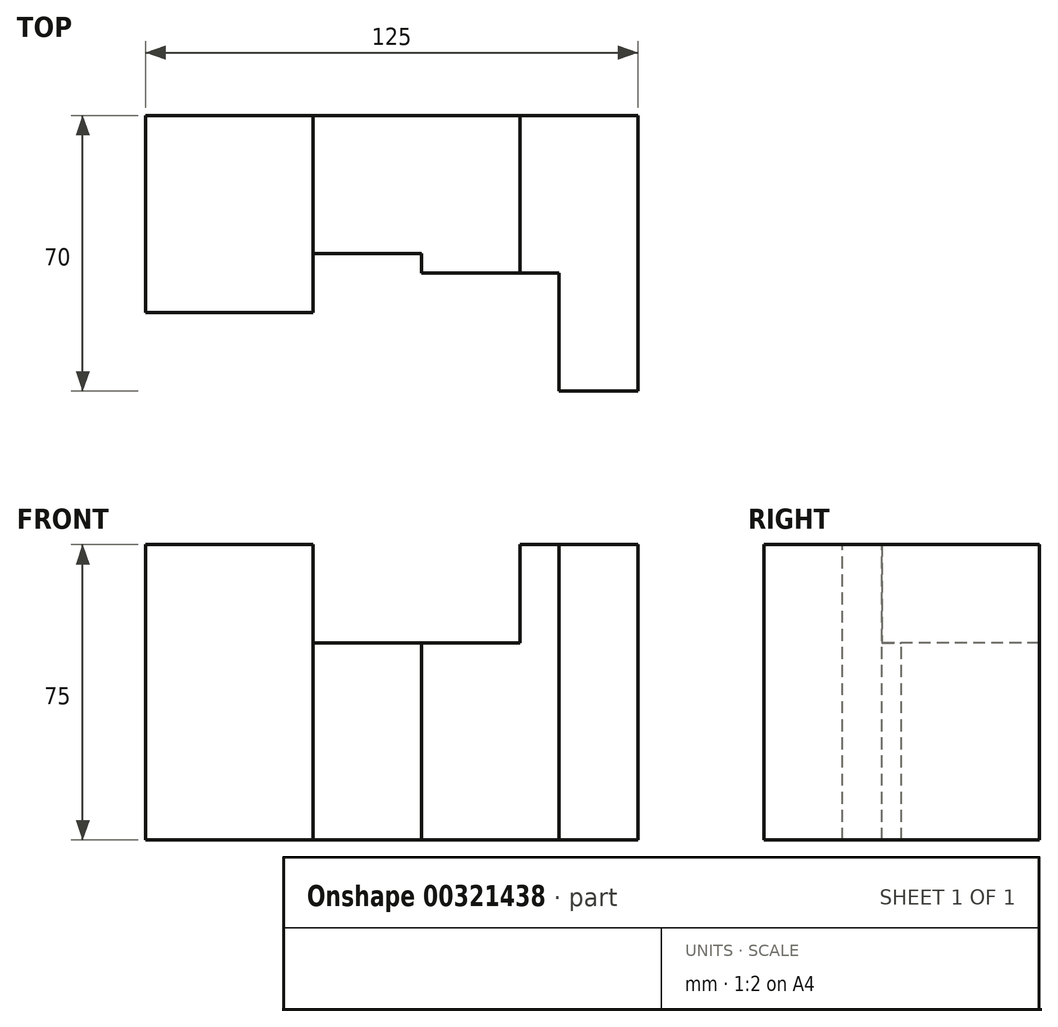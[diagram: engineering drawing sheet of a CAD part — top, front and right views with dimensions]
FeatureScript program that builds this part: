
annotation { "Feature Type Name" : "Feature", "Feature Type Description" : "" }
export const myFeature = defineFeature(function(context is Context, id is Id, definition is map)
    precondition{}
    {
        {
            var Q0;
            Q0=qCreatedBy(makeId("Front.planeOp"),FACE);
            var sketch = newSketch(context, id + "F0", { "sketchPlane" : qUnion([Q0])});
            skLineSegment(sketch, "E0.bottom", {"start": v(0, 0) * mm, "end": v(125, 0) * mm});
            skLineSegment(sketch, "E0.top", {"start": v(0, 75) * mm, "end": v(125, 75) * mm});
            skLineSegment(sketch, "E0.left", {"start": v(0, 0) * mm, "end": v(0, 75) * mm});
            skLineSegment(sketch, "E0.right", {"start": v(125, 0) * mm, "end": v(125, 75) * mm});
            skSolve(sketch);
        }
        {
            var Q0;
            Q0 = qSketchRegion(id + "F0", true);
            extrude(context, id + "F1", {"entities" : qUnion([Q0]), "depth" : (14 * 5) * mm});
        }
        {
            var Q0;
            Q0=makeQuery(id+"F1.opExtrude","SWEPT_FACE",FACE,{"disambiguationData":[OSD([sQuery(id+"F0.wireOp",EDGE,"E0.top")])]});
            var sketch = newSketch(context, id + "F2", { "sketchPlane" : qUnion([Q0])});
            skLineSegment(sketch, "E1.bottom", {"start": v(0, -70) * mm, "end": v(42.5, -70) * mm});
            skLineSegment(sketch, "E1.top", {"start": v(0, -50) * mm, "end": v(42.5, -50) * mm});
            skLineSegment(sketch, "E1.left", {"start": v(0, -70) * mm, "end": v(0, -50) * mm});
            skLineSegment(sketch, "E1.right", {"start": v(42.5, -70) * mm, "end": v(42.5, -50) * mm});
            skSolve(sketch);
        }
        {
            var Q0;
            Q0 = qSketchRegion(id + "F2", true);
            extrude(context, id + "F3", {"entities" : qUnion([Q0]), "operationType" : NewBodyOperationType.REMOVE, "endBound" : BoundingType.THROUGH_ALL, "oppositeDirection" : true, "depth" : 25 * mm});
        }
        {
            var Q0;
            Q0=makeQuery(id+"F1.opExtrude","SWEPT_FACE",FACE,{"disambiguationData":[OSD([sQuery(id+"F0.wireOp",EDGE,"E0.top")])]});
            var sketch = newSketch(context, id + "F4", { "sketchPlane" : qUnion([Q0])});
            skLineSegment(sketch, "E2.bottom", {"start": v(42.5, -50) * mm, "end": v(70, -50) * mm});
            skLineSegment(sketch, "E2.top", {"start": v(42.5, -35) * mm, "end": v(70, -35) * mm});
            skLineSegment(sketch, "E2.left", {"start": v(42.5, -50) * mm, "end": v(42.5, -35) * mm});
            skLineSegment(sketch, "E2.right", {"start": v(70, -50) * mm, "end": v(70, -35) * mm});
            skLineSegment(sketch, "E3.top", {"start": v(42.5, -70) * mm, "end": v(70, -70) * mm});
            skLineSegment(sketch, "E3.left", {"start": v(42.5, -50) * mm, "end": v(42.5, -70) * mm});
            skLineSegment(sketch, "E3.right", {"start": v(70, -50) * mm, "end": v(70, -70) * mm});
            skSolve(sketch);
        }
        {
            var Q0;
            Q0 = qSketchRegion(id + "F4", true);
            extrude(context, id + "F5", {"entities" : qUnion([Q0]), "operationType" : NewBodyOperationType.REMOVE, "endBound" : BoundingType.THROUGH_ALL, "oppositeDirection" : true, "depth" : 25 * mm});
        }
        {
            var Q0;
            Q0=makeQuery(id+"F1.opExtrude","SWEPT_FACE",FACE,{"disambiguationData":[OSD([sQuery(id+"F0.wireOp",EDGE,"E0.top")])]});
            var sketch = newSketch(context, id + "F6", { "sketchPlane" : qUnion([Q0])});
            skLineSegment(sketch, "E4.right", {"start": v(105, -70) * mm, "end": v(105, -40) * mm});
            skLineSegment(sketch, "E5.bottom", {"start": v(105, -70) * mm, "end": v(70, -70) * mm});
            skLineSegment(sketch, "E5.top", {"start": v(105, -40) * mm, "end": v(70, -40) * mm});
            skLineSegment(sketch, "E5.right", {"start": v(70, -70) * mm, "end": v(70, -40) * mm});
            skSolve(sketch);
        }
        {
            var Q0;
            Q0=makeQuery(id+"F6.imprint","IMPRINT",FACE,{"disambiguationData":[TD([[makeQuery(id+"F6.imprint","IMPRINT",EDGE,{"derivedFrom":sQuery(id+"F6.wireOp",EDGE,"E5.bottom")}),1.0]])]});
            extrude(context, id + "F7", {"entities" : qUnion([Q0]), "operationType" : NewBodyOperationType.REMOVE, "endBound" : BoundingType.THROUGH_ALL, "oppositeDirection" : true, "depth" : 25 * mm});
        }
        {
            var Q0;
            Q0=makeQuery(id+"F3.boolean.opBoolean","COPY",FACE,{"derivedFrom":makeQuery(id+"F3.opExtrude","SWEPT_FACE",FACE,{"disambiguationData":[OSD([sQuery(id+"F2.wireOp",EDGE,"E1.top")])]})});
            var sketch = newSketch(context, id + "F8", { "sketchPlane" : qUnion([Q0])});
            skLineSegment(sketch, "E6.bottom", {"start": v(0, 75) * mm, "end": v(25, 75) * mm});
            skLineSegment(sketch, "E6.top", {"start": v(0, 50) * mm, "end": v(25, 50) * mm});
            skLineSegment(sketch, "E6.left", {"start": v(0, 75) * mm, "end": v(0, 50) * mm});
            skLineSegment(sketch, "E6.right", {"start": v(25, 75) * mm, "end": v(25, 50) * mm});
            skLineSegment(sketch, "E7.bottom", {"start": v(25, 50) * mm, "end": v(95, 50) * mm});
            skLineSegment(sketch, "E7.top", {"start": v(25, 75) * mm, "end": v(95, 75) * mm});
            skLineSegment(sketch, "E7.left", {"start": v(25, 50) * mm, "end": v(25, 75) * mm});
            skLineSegment(sketch, "E7.right", {"start": v(95, 50) * mm, "end": v(95, 75) * mm});
            skLineSegment(sketch, "E8.bottom", {"start": v(105, 50) * mm, "end": v(95, 50) * mm});
            skLineSegment(sketch, "E8.top", {"start": v(105, 75) * mm, "end": v(95, 75) * mm});
            skLineSegment(sketch, "E8.left", {"start": v(105, 50) * mm, "end": v(105, 75) * mm});
            skSolve(sketch);
        }
        {
            var Q0;
            {var subQ0=sQuery(id+"F8.wireOp",EDGE,"E7.right");Q0=makeQuery(id+"F8.imprint","IMPRINT",FACE,{"disambiguationData":[TD([[makeQuery(id+"F8.imprint","IMPRINT",EDGE,{"derivedFrom":subQ0}),1.0]])]});}
            var Q1;
            {var subQ0=sQuery(id+"F8.wireOp",EDGE,"E7.left");Q1=makeQuery(id+"F8.imprint","IMPRINT",FACE,{"disambiguationData":[TD([[makeQuery(id+"F8.imprint","IMPRINT",EDGE,{"derivedFrom":subQ0}),-1.0]])]});}
            extrude(context, id + "F9", {"entities" : qUnion([Q0, Q1]), "operationType" : NewBodyOperationType.REMOVE, "endBound" : BoundingType.THROUGH_ALL, "oppositeDirection" : true, "depth" : 25 * mm});
        }
    });
